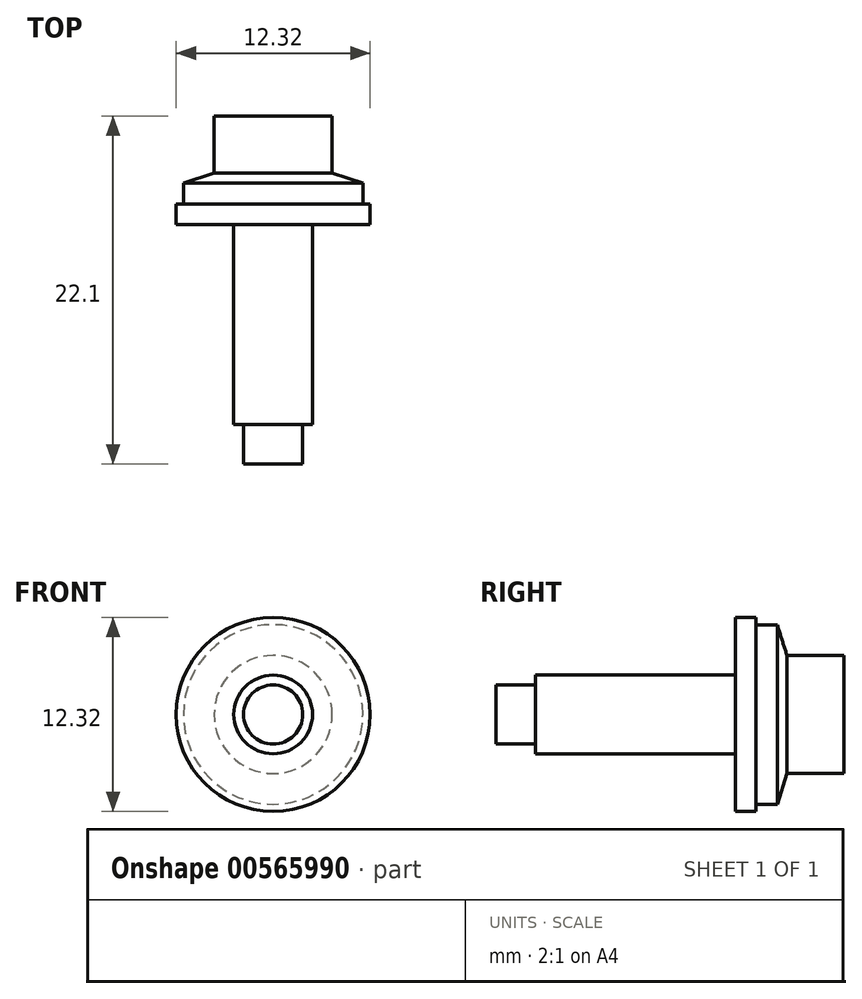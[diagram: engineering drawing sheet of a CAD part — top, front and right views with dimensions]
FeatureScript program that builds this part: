
annotation { "Feature Type Name" : "Feature", "Feature Type Description" : "" }
export const myFeature = defineFeature(function(context is Context, id is Id, definition is map)
    precondition{}
    {
        {
            var Q0;
            Q0=qCreatedBy(makeId("Right.planeOp"),FACE);
            var sketch = newSketch(context, id + "F0", { "sketchPlane" : qUnion([Q0])});
            skLineSegment(sketch, "E0", {"start": v(-15.2, 0) * mm, "end": v(-15.2, -1.88) * mm});
            skLineSegment(sketch, "E1", {"start": v(-15.2, -1.88) * mm, "end": v(-12.7, -1.88) * mm});
            skLineSegment(sketch, "E2", {"start": v(-12.7, -1.88) * mm, "end": v(-12.7, -2.5) * mm});
            skLineSegment(sketch, "E3", {"start": v(-12.7, -2.5) * mm, "end": v(0, -2.5) * mm});
            skLineSegment(sketch, "E4", {"start": v(0, -2.5) * mm, "end": v(0, -6.16) * mm});
            skLineSegment(sketch, "E5", {"start": v(0, -6.16) * mm, "end": v(1.3, -6.16) * mm});
            skLineSegment(sketch, "E6", {"start": v(1.3, -6.16) * mm, "end": v(1.3, -5.7) * mm});
            skLineSegment(sketch, "E7", {"start": v(1.3, -5.7) * mm, "end": v(2.66, -5.7) * mm});
            skLineSegment(sketch, "E8", {"start": v(6.9, 0) * mm, "end": v(-15.2, 0) * mm});
            skLineSegment(sketch, "E9", {"start": v(2.66, -5.7) * mm, "end": v(3.27, -3.75) * mm});
            skLineSegment(sketch, "E10", {"start": v(3.27, -3.75) * mm, "end": v(6.9, -3.75) * mm});
            skLineSegment(sketch, "E11", {"start": v(6.9, -3.75) * mm, "end": v(6.9, 0) * mm});
            skSolve(sketch);
        }
        {
            var Q0;
            Q0 = qSketchRegion(id + "F0", true);
            var Q1;
            Q1=sQuery(id+"F0.wireOp",EDGE,"E8");
            revolve(context, id + "F1", {"surfaceOperationType" : NewSurfaceOperationType.NEW, "entities" : qUnion([Q0]), "axis" : qUnion([Q1]), "revolveType" : RevolveType.FULL});
        }
    });
